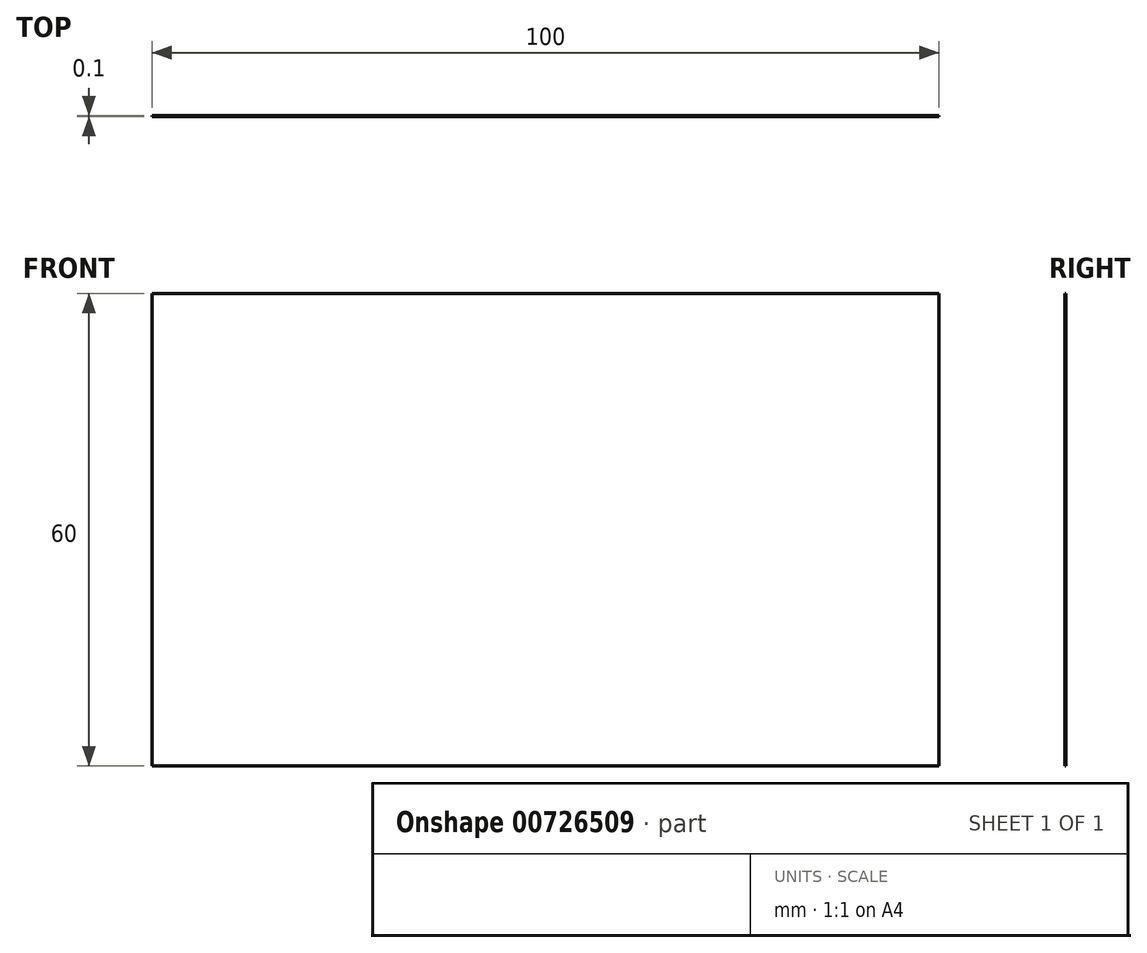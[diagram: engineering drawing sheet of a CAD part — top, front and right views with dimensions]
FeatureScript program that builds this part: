
annotation { "Feature Type Name" : "Feature", "Feature Type Description" : "" }
export const myFeature = defineFeature(function(context is Context, id is Id, definition is map)
    precondition{}
    {
        {
            var Q0;
            Q0=qCreatedBy(makeId("Front.planeOp"),FACE);
            var sketch = newSketch(context, id + "F0", { "sketchPlane" : qUnion([Q0])});
            skLineSegment(sketch, "E0.top", {"start": v(-50, -30) * mm, "end": v(50, -30) * mm});
            skLineSegment(sketch, "E0.left", {"start": v(-50, 30) * mm, "end": v(-50, -30) * mm});
            skLineSegment(sketch, "E0.right", {"start": v(50, 30) * mm, "end": v(50, -30) * mm});
            skPoint(sketch, "E0.middle", {"position": v(0, 0) * mm});
            skLineSegment(sketch, "E1", {"start": v(-50, 30) * mm, "end": v(50, 30) * mm});
            skSolve(sketch);
        }
        {
            var Q0;
            Q0 = qSketchRegion(id + "F0", true);
            extrude(context, id + "F1", {"entities" : qUnion([Q0]), "depth" : 0.1 * mm, "offsetDistance" : 25 * mm});
        }
    });
